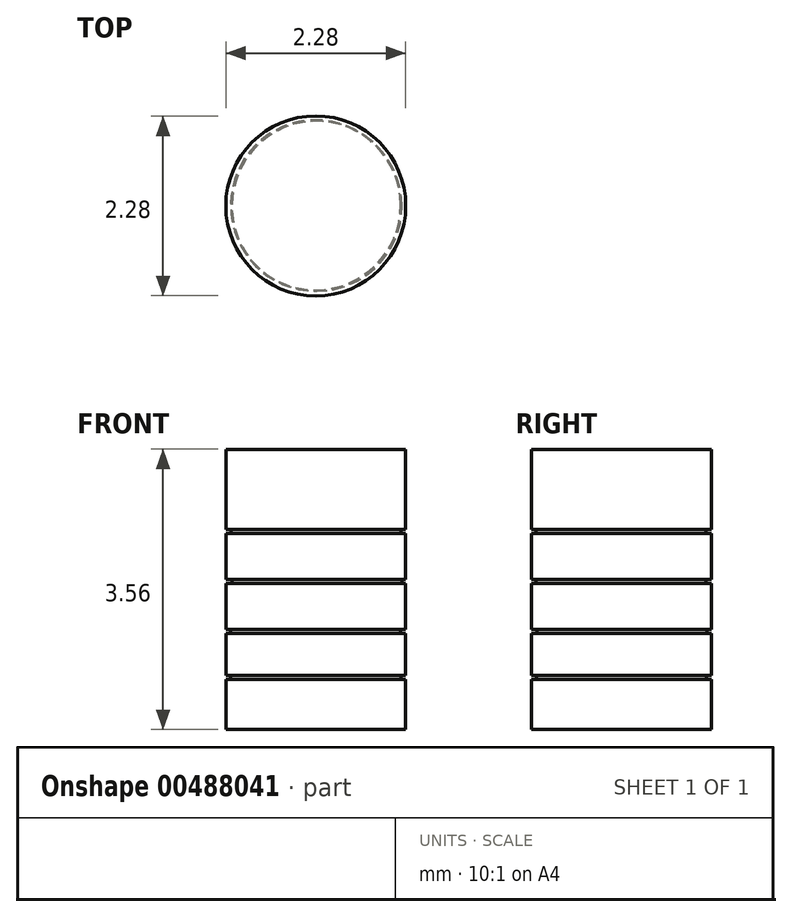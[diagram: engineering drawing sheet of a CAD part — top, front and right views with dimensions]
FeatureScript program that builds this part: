
annotation { "Feature Type Name" : "Feature", "Feature Type Description" : "" }
export const myFeature = defineFeature(function(context is Context, id is Id, definition is map)
    precondition{}
    {
        {
            var Q0;
            Q0=qCreatedBy(makeId("Top.planeOp"),FACE);
            var sketch = newSketch(context, id + "F0", { "sketchPlane" : qUnion([Q0])});
            skCircle(sketch, "E0", {"center": v(0, 0) * mm, "radius": 1.14 * mm});
            skSolve(sketch);
        }
        {
            var Q0;
            Q0=qSketchRegion(id+"F0",true);
            extrude(context, id + "F1", {"entities" : qUnion([Q0]), "depth" : 3.56 * mm, "offsetDistance" : 25.4 * mm});
        }
        {
            var Q0;
            Q0=qCreatedBy(makeId("Top.planeOp"),FACE);
            cPlane(context, id + "F2", {"entities" : qUnion([Q0]), "cplaneType" : CPlaneType.OFFSET, "offset" : 0.64 * mm, "width" : 152.4 * mm, "height" : 152.4 * mm});
        }
        {
            var Q0;
            Q0=qCreatedBy(id+"F2.planeOp",FACE);
            cPlane(context, id + "F3", {"entities" : qUnion([Q0]), "cplaneType" : CPlaneType.OFFSET, "offset" : 0.64 * mm, "width" : 152.4 * mm, "height" : 152.4 * mm});
        }
        {
            var Q0;
            Q0=qCreatedBy(id+"F3.planeOp",FACE);
            cPlane(context, id + "F4", {"entities" : qUnion([Q0]), "cplaneType" : CPlaneType.OFFSET, "offset" : 0.64 * mm, "width" : 152.4 * mm, "height" : 152.4 * mm});
        }
        {
            var Q0;
            Q0=qCreatedBy(id+"F4.planeOp",FACE);
            cPlane(context, id + "F5", {"entities" : qUnion([Q0]), "cplaneType" : CPlaneType.OFFSET, "offset" : 0.64 * mm, "width" : 152.4 * mm, "height" : 152.4 * mm});
        }
        {
            var Q0;
            Q0=qCreatedBy(id+"F2.planeOp",FACE);
            var sketch = newSketch(context, id + "F6", { "sketchPlane" : qUnion([Q0])});
            skCircle(sketch, "E1", {"center": v(0, 0) * mm, "radius": 1.08 * mm});
            skCircle(sketch, "E2", {"center": v(0, 0) * mm, "radius": 1.14 * mm});
            skSolve(sketch);
        }
        {
            var Q0;
            Q0=qSketchRegion(id+"F6",true);
            extrude(context, id + "F7", {"entities" : qUnion([Q0]), "operationType" : NewBodyOperationType.REMOVE, "depth" : 0.05 * mm, "offsetDistance" : 25.4 * mm});
        }
        {
            var Q0;
            Q0=qCreatedBy(id+"F3.planeOp",FACE);
            var sketch = newSketch(context, id + "F8", { "sketchPlane" : qUnion([Q0])});
            skCircle(sketch, "E3", {"center": v(0, 0.01) * mm, "radius": 1.08 * mm});
            skCircle(sketch, "E4", {"center": v(0, 0.01) * mm, "radius": 1.16 * mm});
            skSolve(sketch);
        }
        {
            var Q0;
            Q0=qSketchRegion(id+"F8",true);
            var Q1;
            Q1=qConstructionFilter(qBodyType(qCreatedBy(id+"F8",EDGE),BodyType.WIRE),ConstructionObject.NO);
            extrude(context, id + "F9", {"entities" : qUnion([Q0]), "operationType" : NewBodyOperationType.REMOVE, "surfaceEntities" : qUnion([Q1]), "oppositeDirection" : true, "depth" : 0.05 * mm, "offsetDistance" : 25.4 * mm});
        }
        {
            var Q0;
            Q0=qCreatedBy(id+"F4.planeOp",FACE);
            var sketch = newSketch(context, id + "F10", { "sketchPlane" : qUnion([Q0])});
            skCircle(sketch, "E5", {"center": v(0.02, 0) * mm, "radius": 1.08 * mm});
            skCircle(sketch, "E6", {"center": v(0.02, 0) * mm, "radius": 1.17 * mm});
            skSolve(sketch);
        }
        {
            var Q0;
            Q0=qSketchRegion(id+"F10",true);
            extrude(context, id + "F11", {"entities" : qUnion([Q0]), "operationType" : NewBodyOperationType.REMOVE, "oppositeDirection" : true, "depth" : 0.05 * mm, "offsetDistance" : 25.4 * mm});
        }
        {
            var Q0;
            Q0=qCreatedBy(id+"F5.planeOp",FACE);
            var sketch = newSketch(context, id + "F12", { "sketchPlane" : qUnion([Q0])});
            skCircle(sketch, "E7", {"center": v(0, 0) * mm, "radius": 1.08 * mm});
            skCircle(sketch, "E8", {"center": v(0, 0) * mm, "radius": 1.16 * mm});
            skSolve(sketch);
        }
        {
            var Q0;
            Q0=qSketchRegion(id+"F12",true);
            var Q1;
            Q1=qConstructionFilter(qBodyType(qCreatedBy(id+"F12",EDGE),BodyType.WIRE),ConstructionObject.NO);
            extrude(context, id + "F13", {"entities" : qUnion([Q0]), "operationType" : NewBodyOperationType.REMOVE, "surfaceEntities" : qUnion([Q1]), "oppositeDirection" : true, "depth" : 0.05 * mm, "offsetDistance" : 25.4 * mm});
        }
    });
